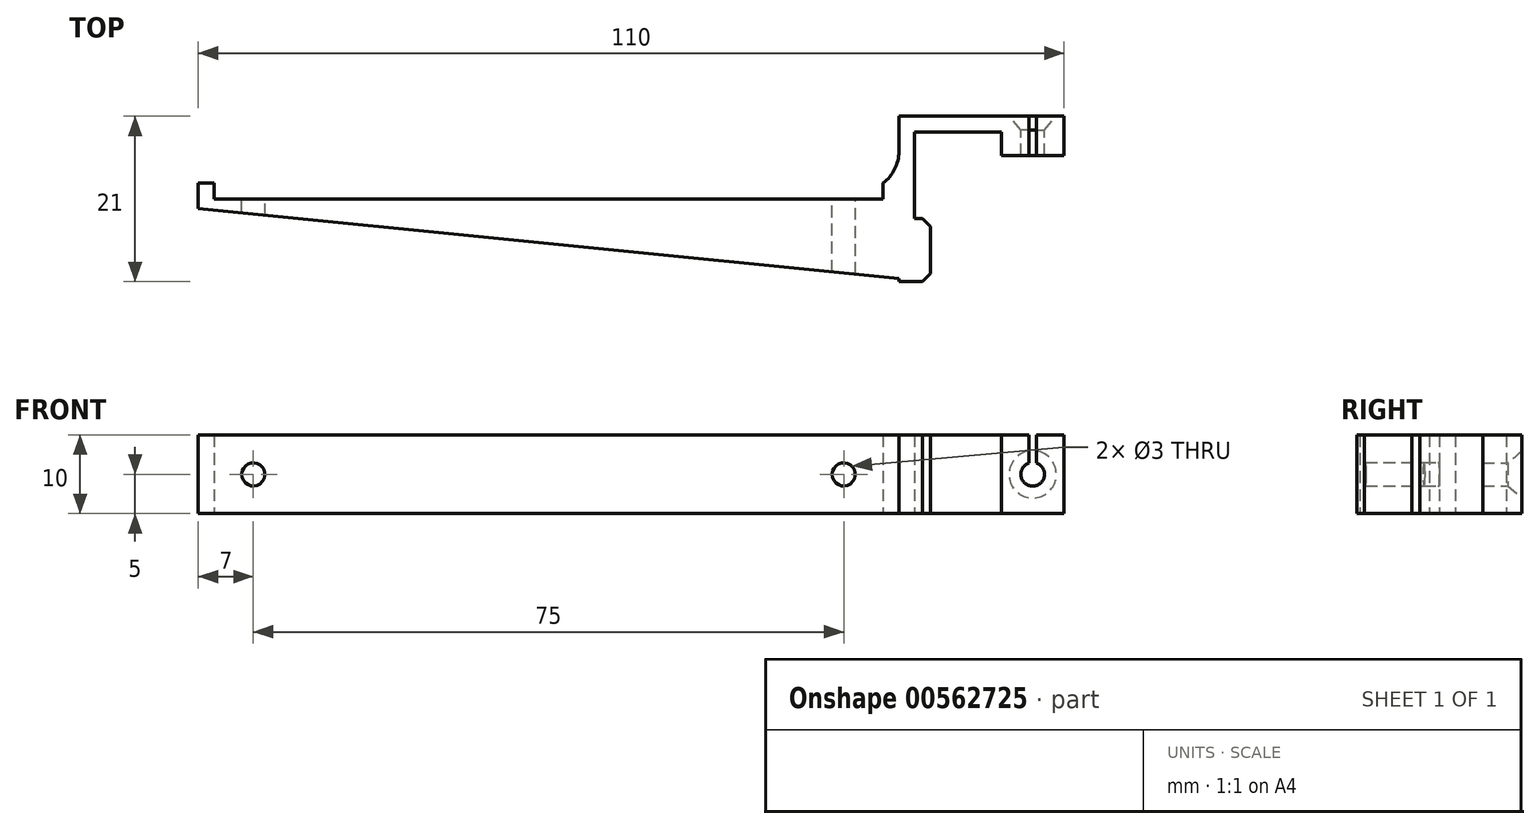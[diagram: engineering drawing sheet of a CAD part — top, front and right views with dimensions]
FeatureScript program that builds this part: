
annotation { "Feature Type Name" : "Feature", "Feature Type Description" : "" }
export const myFeature = defineFeature(function(context is Context, id is Id, definition is map)
    precondition{}
    {
        {
            var Q0;
            Q0=qCreatedBy(makeId("Top.planeOp"),FACE);
            var sketch = newSketch(context, id + "F0", { "sketchPlane" : qUnion([Q0])});
            skLineSegment(sketch, "E0", {"start": v(13, 16) * mm, "end": v(21, 16) * mm});
            skLineSegment(sketch, "E1", {"start": v(21, 16) * mm, "end": v(21, 21) * mm});
            skLineSegment(sketch, "E2", {"start": v(21, 21) * mm, "end": v(0, 21) * mm});
            skLineSegment(sketch, "E3", {"start": v(0, 21) * mm, "end": v(0, 10.5) * mm});
            skLineSegment(sketch, "E4", {"start": v(13, 16) * mm, "end": v(13, 19) * mm});
            skLineSegment(sketch, "E5", {"start": v(13, 19) * mm, "end": v(2, 19) * mm});
            skLineSegment(sketch, "E6", {"start": v(2, 19) * mm, "end": v(2, 8) * mm});
            skLineSegment(sketch, "E7", {"start": v(2, 8) * mm, "end": v(4, 8) * mm});
            skLineSegment(sketch, "E8", {"start": v(4, 8) * mm, "end": v(4, 0) * mm});
            skLineSegment(sketch, "E9", {"start": v(4, 0) * mm, "end": v(0, 0) * mm});
            skLineSegment(sketch, "E10", {"start": v(0, 10.5) * mm, "end": v(0, 10.5) * mm});
            skLineSegment(sketch, "E11", {"start": v(0, 10.5) * mm, "end": v(0, 12.5) * mm});
            skLineSegment(sketch, "E12", {"start": v(0, 12.5) * mm, "end": v(-2, 12.5) * mm});
            skLineSegment(sketch, "E13", {"start": v(-2, 12.5) * mm, "end": v(-2, 10.5) * mm});
            skLineSegment(sketch, "E14", {"start": v(-2, 10.5) * mm, "end": v(-87, 10.5) * mm});
            skLineSegment(sketch, "E15", {"start": v(-87, 10.5) * mm, "end": v(-87, 12.5) * mm});
            skLineSegment(sketch, "E16", {"start": v(-87, 12.5) * mm, "end": v(-89, 12.5) * mm});
            skLineSegment(sketch, "E17", {"start": v(-89, 12.5) * mm, "end": v(-89, 10.5) * mm});
            skLineSegment(sketch, "E18", {"start": v(-89, 10.5) * mm, "end": v(-89, 9.24) * mm});
            skLineSegment(sketch, "E19", {"start": v(-89, 9.24) * mm, "end": v(4, 0) * mm});
            skLineSegment(sketch, "E20.trimOffspring", {"start": v(0, 0.4) * mm, "end": v(0, 0) * mm});
            skSolve(sketch);
        }
        {
            var Q0;
            Q0 = qSketchRegion(id + "F0", true);
            extrude(context, id + "F1", {"entities" : qUnion([Q0]), "depth" : 10 * mm, "offsetDistance" : 25 * mm});
        }
        {
            var Q0;
            Q0=makeQuery(id+"F1.opExtrude","SWEPT_FACE",FACE,{"disambiguationData":[OSD([sQuery(id+"F0.wireOp",EDGE,"E14")])]});
            var sketch = newSketch(context, id + "F2", { "sketchPlane" : qUnion([Q0])});
            skCircle(sketch, "E21", {"center": v(82, 5) * mm, "radius": 1.5 * mm});
            skPoint(sketch, "E21.centerSnap0", {"position": v(87, 5) * mm});
            skCircle(sketch, "E22", {"center": v(7, 5) * mm, "radius": 1.5 * mm});
            skArc(sketch, "E23", {"start": v(-17.5, 6.41) * mm, "mid": v(-17, 3.5) * mm, "end": v(-16.5, 6.41) * mm});
            skPoint(sketch, "E23.centerSnap0", {"position": v(2, 5) * mm});
            skLineSegment(sketch, "E24", {"start": v(-16.5, 10.77) * mm, "end": v(-16.5, 6.41) * mm});
            skLineSegment(sketch, "E25", {"start": v(-17.5, 10.77) * mm, "end": v(-17.5, 6.41) * mm});
            skLineSegment(sketch, "E26", {"start": v(-17.5, 10.77) * mm, "end": v(-16.5, 10.77) * mm});
            skPoint(sketch, "E27.orphan", {"position": v(-16.5, 10.9) * mm});
            skPoint(sketch, "E28.orphan", {"position": v(-16.5, 5) * mm});
            skSolve(sketch);
        }
        {
            var Q0;
            Q0 = qSketchRegion(id + "F2", true);
            extrude(context, id + "F3", {"entities" : qUnion([Q0]), "operationType" : NewBodyOperationType.REMOVE, "oppositeDirection" : true, "depth" : 25 * mm, "offsetDistance" : 25 * mm, "hasSecondDirection" : true, "secondDirectionOppositeDirection" : false, "secondDirectionDepth" : 25 * mm});
        }
        {
            var Q0;
            Q0=makeQuery(id+"F3.boolean.opBoolean","INTERSECT",EDGE,{"derivedFrom":[makeQuery(id+"F1.opExtrude","SWEPT_FACE",FACE,{"disambiguationData":[OSD([sQuery(id+"F0.wireOp",EDGE,"E2")])]}),makeQuery(id+"F3.opExtrude","SWEPT_FACE",FACE,{"disambiguationData":[OSD([sQuery(id+"F2.wireOp",EDGE,"E23")])]})]});
            chamfer(context, id + "F4", {"entities" : qUnion([Q0]), "chamferType" : ChamferType.OFFSET_ANGLE, "width" : 1.5 * mm, "oppositeDirection" : false, "angle" : 50 * degree, "tangentPropagation" : true});
        }
        {
            var Q0;
            Q0=makeQuery(id+"F1.opExtrude","SWEPT_EDGE",EDGE,{"disambiguationData":[OSD([sQuery(id+"F0.wireOp",EDGE,"E3"),sQuery(id+"F0.wireOp",EDGE,"E12")])]});
            fillet(context, id + "F5", {"entities" : qUnion([Q0]), "radius" : 5 * mm, "tangentPropagation" : true, "allowEdgeOverflow" : false});
        }
        {
            var Q0;
            Q0=makeQuery(id+"F1.opExtrude","SWEPT_EDGE",EDGE,{"disambiguationData":[OSD([sQuery(id+"F0.wireOp",EDGE,"E7"),sQuery(id+"F0.wireOp",EDGE,"E8")])]});
            chamfer(context, id + "F6", {"entities" : qUnion([Q0]), "width" : 1 * mm, "tangentPropagation" : true});
        }
        {
            var Q0;
            Q0=makeQuery(id+"F1.opExtrude","SWEPT_EDGE",EDGE,{"disambiguationData":[OSD([sQuery(id+"F0.wireOp",EDGE,"E8"),sQuery(id+"F0.wireOp",EDGE,"E9"),sQuery(id+"F0.wireOp",EDGE,"E19")])]});
            chamfer(context, id + "F7", {"entities" : qUnion([Q0]), "width" : 1 * mm, "tangentPropagation" : true});
        }
    });
